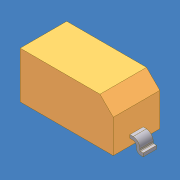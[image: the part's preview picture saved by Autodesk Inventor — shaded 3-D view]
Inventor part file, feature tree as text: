
AUTODESK INVENTOR PART (.ipt)
format: ipt  version: 2012 (Build 160160000, 160)  size: 131,584 bytes
history: native  units: mm (DEFAULTED — no unit token found)
features: sketch x3, extrude x1, chamfer x1, plane x1, sweep x1, mirror x1
ambient origin geometry x8: Origin, YZ Plane, XZ Plane, XY Plane, X Axis, Y Axis, Z Axis, Center Point
bodies: Solid1 (feature_tree)
feature tree (8):
  extrude  "Extrusion1"  Depth=3.5mm
  chamfer  "Chamfer1"  Distance=1.75mm
  sketch  "Sketch2"  dims[d4=0.5mm d5=2.0mm d6=0.25mm]
  plane  "Work Plane2"
  sweep  "Sweep1"
  mirror  "Mirror1"
  sketch  "Sketch1"  dims[d0=1.75mm d1=3.5mm d2=1.75mm d3=0.0mm]
  sketch  "Sketch4"  dims[d7=0.5mm d8=0.125mm d10=90.0deg d11=0.25mm d12=0.25mm d13=0.35mm d14=0.15mm d15=0.0mm d16=45.0deg]
